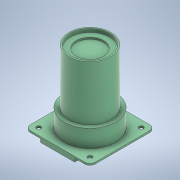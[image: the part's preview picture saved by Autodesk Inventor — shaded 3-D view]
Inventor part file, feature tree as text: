
AUTODESK INVENTOR PART (.ipt)
format: ipt  version: 2021 (Build 250183000, 183)  size: 211,456 bytes
history: native  units: mm
features: sketch x6, extrude x5, fillet x1, revolve x1
ambient origin geometry x8: Origin, YZ Plane, XZ Plane, XY Plane, X Axis, Y Axis, Z Axis, Center Point
bodies: Solid1 (feature_tree)
feature tree (13):
  extrude  "Extrusion1"  Depth=38.0mm
  fillet  "Fillet1"  Radius=30.0mm
  revolve  "Revolution1"  [1 undecoded]
  extrude  "Extrusion2"  Depth=2.5mm
  extrude  "Extrusion3"  Depth=1.0mm TaperAngle=0.0deg
  extrude  "Extrusion4"  TaperAngle=90.0deg  [1 undecoded]
  extrude  "Extrusion5"  Depth=2.0mm
  sketch  "Sketch1"  dims[d0=38.0mm d1=38.0mm d2=30.0mm]
  sketch  "Sketch2"  dims[d3=30.0mm d4=2.5mm]
  sketch  "Sketch3"  dims[d5=2.5mm d6=2.5mm]
  sketch  "Sketch4"  dims[d7=2.5mm d8=1.0mm d9=0.0mm]
  sketch  "Sketch5"  dims[d10=3.0mm d15=90.0deg]
  sketch  "Sketch6"  dims[d16=15.0mm d17=10.2mm d18=2.5mm d19=32.0mm d20=23.0mm d21=2.0mm d22=0.0mm d23=16.0mm d24=1.0mm d25=0.0mm d26=5.0mm d27=7.0mm d28=5.0mm d29=7.0mm d30=3.0mm d31=0.0mm d32=20.0mm d33=5.5mm d34=2.0mm d35=0.0mm]
note: 2 required parameter values undecoded (feature->parameter linkage not recoverable at this tier; creation-order binding heuristic only, values carry confidence <= 0.55)